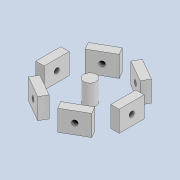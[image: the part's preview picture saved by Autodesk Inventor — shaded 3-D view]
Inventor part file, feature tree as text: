
AUTODESK INVENTOR PART (.ipt)
format: ipt  version: 2020 (Build 240168000, 168)  size: 125,952 bytes
history: native  units: mm
features: extrude x3, sketch x3, pattern_circular x2, projected_geometry x1
ambient origin geometry x8: Origin, YZ Plane, XZ Plane, XY Plane, X Axis, Y Axis, Z Axis, Center Point
bodies: Solid1 (feature_tree)
feature tree (9):
  extrude  "Extrusion1"  Depth=5.0mm TaperAngle=0.0deg
  extrude  "Extrusion2"  Depth=10.0mm
  pattern_circular  "Circular Pattern1"  [2 undecoded]
  extrude  "Extrusion3"  Depth=5.0mm TaperAngle=0.0deg
  pattern_circular  "Circular Pattern2"  Count=6 Angle=360.0deg
  sketch  "Sketch1"  dims[d0=3.0mm d1=5.0mm d2=0.0mm]
  sketch  "Sketch2"  dims[d3=10.0mm d4=1.0mm]
  sketch  "Sketch3"  dims[d5=2.0mm d6=6.0mm d7=5.0mm d8=0.0mm d9=60.0mm d10=360.0deg d12=3.0mm d13=1.2mm d14=5.0mm d15=0.0mm d16=60.0mm d17=360.0deg]
  projected_geometry  "Projected Loop1"
note: 2 required parameter values undecoded (feature->parameter linkage not recoverable at this tier; creation-order binding heuristic only, values carry confidence <= 0.55)
